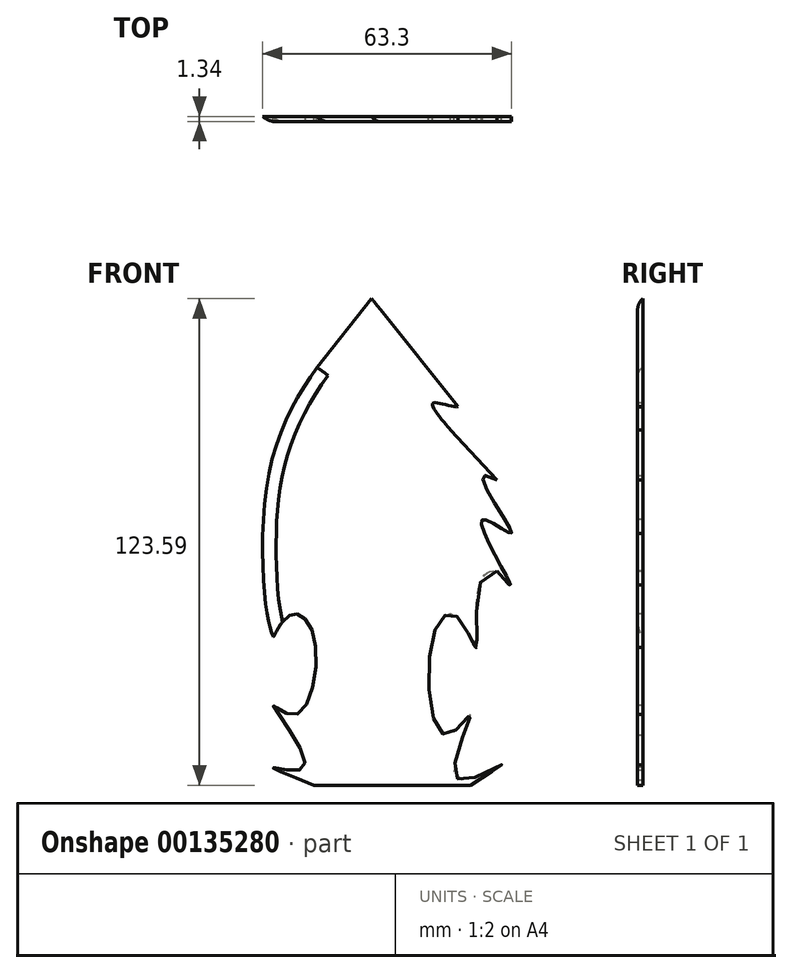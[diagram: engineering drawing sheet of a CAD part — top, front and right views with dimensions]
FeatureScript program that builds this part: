
annotation { "Feature Type Name" : "Feature", "Feature Type Description" : "" }
export const myFeature = defineFeature(function(context is Context, id is Id, definition is map)
    precondition{}
    {
        {
            var Q0;
            Q0=qCreatedBy(makeId("Front.planeOp"),FACE);
            var sketch = newSketch(context, id + "F0", { "sketchPlane" : qUnion([Q0])});
            skFitSpline(sketch, "E0", {"points": [v(-22, 49.46) * mm, v(-34.08, 23.2) * mm, v(-34.86, -12.05) * mm, v(-33.1, -19.1) * mm], "startDerivative": vector(-38.28, -55.13) * mm, "endDerivative": vector(10.1, -27.94) * mm});
            skFitSpline(sketch, "E1", {"points": [v(-33.1, -19.1) * mm, v(-28.2, -13.22) * mm, v(-22.72, -19.1) * mm, v(-27.81, -38.88) * mm, v(-33.1, -36.53) * mm, v(-25.27, -52) * mm, v(-33.1, -52.2) * mm, v(-22.72, -56.7) * mm], "startDerivative": vector(36.55, 67.8) * mm, "endDerivative": vector(118, -47.08) * mm});
            skLineSegment(sketch, "E2", {"start": v(-22.72, -56.7) * mm, "end": v(17.04, -56.7) * mm});
            skFitSpline(sketch, "E3", {"points": [v(17.04, -56.7) * mm, v(24.68, -51.6) * mm, v(13.32, -54.74) * mm, v(17.04, -38.68) * mm, v(10.97, -43.97) * mm, v(7.44, -18.9) * mm, v(13.51, -13.8) * mm, v(18.6, -21.64) * mm, v(23.7, -2.25) * mm], "startDerivative": vector(144.74, 93.28) * mm, "endDerivative": vector(147, -21.15) * mm});
            skFitSpline(sketch, "E4", {"points": [v(23.7, -2.25) * mm, v(27.03, -5.39) * mm, v(20.17, 10.87) * mm, v(27.42, 7.74) * mm, v(23.7, 20.86) * mm], "startDerivative": vector(44.65, -50.73) * mm, "endDerivative": vector(100.47, -57.13) * mm});
            skLineSegment(sketch, "E5", {"start": v(23.7, 20.86) * mm, "end": v(11.88, 33.6) * mm});
            skFitSpline(sketch, "E6", {"points": [v(11.88, 33.6) * mm, v(7.38, 40.25) * mm, v(13.84, 39.47) * mm], "startDerivative": vector(-4.98, 6.61) * mm, "endDerivative": vector(8.25, 2.27) * mm});
            skLineSegment(sketch, "E7", {"start": v(-22, 49.46) * mm, "end": v(-8.1, 66.9) * mm});
            skLineSegment(sketch, "E8", {"start": v(-8.1, 66.9) * mm, "end": v(13.84, 39.47) * mm});
            skSolve(sketch);
        }
        {
            var Q0;
            Q0=makeQuery(id+"F0.imprint","IMPRINT",FACE,{"disambiguationData":[TD([[makeQuery(id+"F0.imprint","IMPRINT",EDGE,{"derivedFrom":sQuery(id+"F0.wireOp",EDGE,"E0")}),1.0]])]});
            extrude(context, id + "F1", {"entities" : qUnion([Q0]), "depth" : 1.34 * mm});
        }
        {
            var Q0;
            Q0=makeQuery(id+"F1.opExtrude","CAP_EDGE",EDGE,{"disambiguationData":[OSD([sQuery(id+"F0.wireOp",EDGE,"E7")])],"isStart":false});
            var Q1;
            Q1=makeQuery(id+"F1.opExtrude","CAP_EDGE",EDGE,{"disambiguationData":[OSD([sQuery(id+"F0.wireOp",EDGE,"E0")])],"isStart":false});
            fillet(context, id + "F2", {"entities" : qUnion([Q0, Q1]), "radius" : 5.08 * mm, "tangentPropagation" : true, "allowEdgeOverflow" : false});
        }
    });
